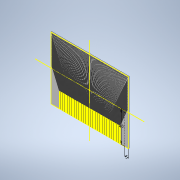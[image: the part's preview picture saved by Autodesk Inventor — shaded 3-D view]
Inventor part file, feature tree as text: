
AUTODESK INVENTOR PART (.ipt)
format: ipt  version: 2021 (Build 250183000, 183)  size: 3,146,240 bytes
history: native  units: in
note: dims shown in document units (in); Inventor stores cm internally (conversion verified against a paired STEP export)
features: sketch x6, extrude x5, projected_geometry x5, pattern_linear x3, mirror x2
ambient origin geometry x8: Origin, YZ Plane, XZ Plane, XY Plane, X Axis, Y Axis, Z Axis, Center Point
bodies: Solid1 (feature_tree)
feature tree (21):
  extrude  "Extrusion1"  Depth=3.1496in
  extrude  "Extrusion2"  Depth=0.0118in
  pattern_linear  "Rectangular Pattern1"  Count1=2  [1 undecoded]
  sketch  "Sketch3"  dims[d6=0.0014in d7=0.0in d8=51.5748in d10=0.0236in d11=1.5748in]
  extrude  "Extrusion3"  Depth=0.0236in
  pattern_linear  "Rectangular Pattern2"  Count1=4  [1 undecoded]
  extrude  "Extrusion4"  Depth=0.0394in
  pattern_linear  "Rectangular Pattern3"  Count1=77 Spacing1=0.05in
  mirror  "Mirror1"
  extrude  "Extrusion5"  Depth=0.0014in
  mirror  "Mirror2"
  sketch  "Sketch1"  dims[d0=3.937in d1=3.1496in]
  sketch  "Sketch2"  dims[d2=0.0394in d3=0.0in d4=0.0118in d5=0.7874in]
  projected_geometry  "Projected Loop1"
  projected_geometry  "Projected Loop2"
  sketch  "Sketch4"  dims[d12=0.1969in d13=0.0394in]
  projected_geometry  "Projected Loop3"
  sketch  "Sketch5"  dims[d14=0.0591in]
  projected_geometry  "Projected Loop4"
  sketch  "Sketch7"  dims[d15=0.0014in d16=0.0in d17=30.315in d19=0.05in d20=0.3937in d22=0.05in d23=0.0157in d24=0.0591in d25=0.1083in d26=0.0014in d27=0.0in d28=10.6299in d30=0.05in d35=0.0118in d36=0.0118in d37=0.0118in d38=0.0118in d39=0.0118in d40=0.0118in d41=0.0118in d42=0.0118in d43=0.0118in d44=0.0118in d45=0.0118in d46=0.0118in d47=0.0118in d48=0.0118in d49=0.0118in d50=0.0118in d51=0.0118in d52=0.0118in d53=0.0118in d54=0.0118in d55=0.0118in d56=0.0118in d57=0.0118in d58=0.0118in d59=0.0118in d60=0.0118in d61=0.0118in d62=0.0118in d63=0.0118in d64=0.0118in d65=0.0118in d66=0.0118in d67=0.0118in d68=0.0118in d69=0.0118in d70=0.0118in d71=0.0118in d72=0.0118in d73=0.0118in d74=0.0118in d75=0.0118in d76=0.0118in d77=0.0118in d78=0.0118in d79=0.0118in d80=0.0118in d81=0.0118in d82=0.0118in d83=0.0118in d84=0.0118in d85=0.0118in d86=0.0118in d87=0.0118in d88=0.0118in d89=0.0118in d90=0.0118in d91=0.0118in d92=0.0118in d93=0.0118in d94=0.0118in d95=0.0118in d96=0.0118in d97=0.0118in d98=0.0118in d99=0.0118in d100=0.0118in d101=0.0014in d102=0.0in]
  projected_geometry  "Projected Loop6"
note: 2 required parameter values undecoded (feature->parameter linkage not recoverable at this tier; creation-order binding heuristic only, values carry confidence <= 0.55)
